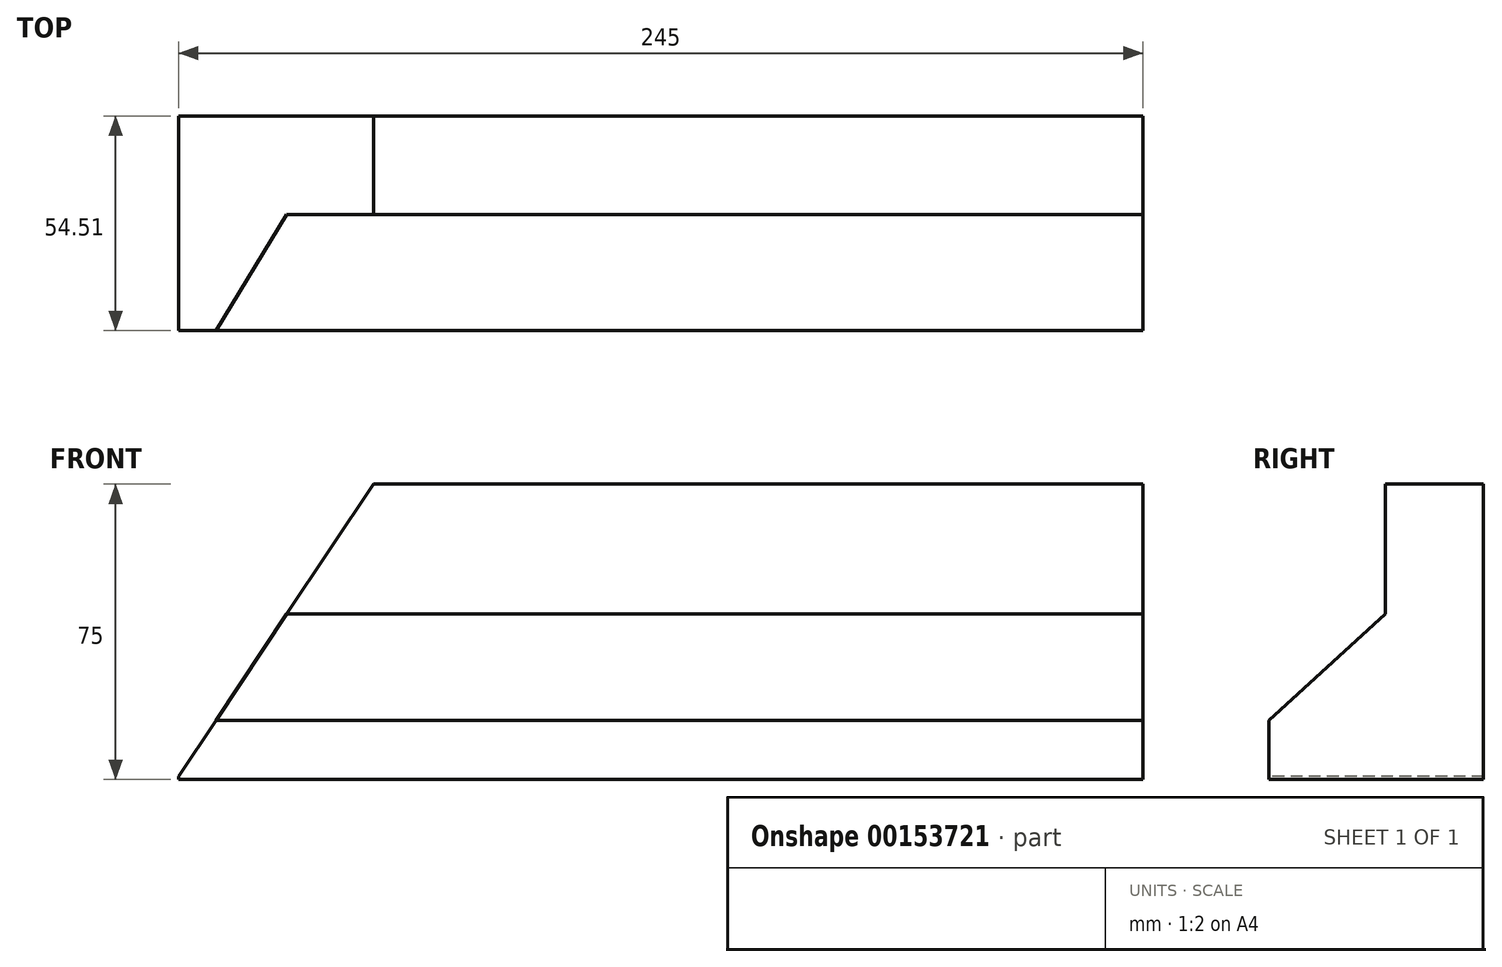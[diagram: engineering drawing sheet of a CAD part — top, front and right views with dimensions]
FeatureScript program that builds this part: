
annotation { "Feature Type Name" : "Feature", "Feature Type Description" : "" }
export const myFeature = defineFeature(function(context is Context, id is Id, definition is map)
    precondition{}
    {
        {
            var Q0;
            Q0=qCreatedBy(makeId("Right.planeOp"),FACE);
            var sketch = newSketch(context, id + "F0", { "sketchPlane" : qUnion([Q0])});
            skLineSegment(sketch, "E0.bottom", {"start": v(-15.45, 41.87) * mm, "end": v(9.55, 41.87) * mm});
            skLineSegment(sketch, "E0.top", {"start": v(-15.45, -33.13) * mm, "end": v(9.55, -33.13) * mm});
            skLineSegment(sketch, "E0.left", {"start": v(-15.45, 41.87) * mm, "end": v(-15.45, -33.13) * mm});
            skLineSegment(sketch, "E0.right", {"start": v(9.55, 41.87) * mm, "end": v(9.55, -33.13) * mm});
            skLineSegment(sketch, "E1.bottom", {"start": v(9.55, -33.13) * mm, "end": v(-44.96, -33.13) * mm});
            skLineSegment(sketch, "E1.top", {"start": v(9.55, -18.13) * mm, "end": v(-44.96, -18.13) * mm});
            skLineSegment(sketch, "E1.left", {"start": v(9.55, -33.13) * mm, "end": v(9.55, -18.13) * mm});
            skLineSegment(sketch, "E1.right", {"start": v(-44.96, -33.13) * mm, "end": v(-44.96, -18.13) * mm});
            skLineSegment(sketch, "E2", {"start": v(-15.45, 8.87) * mm, "end": v(-44.96, -18.13) * mm});
            skSolve(sketch);
        }
        {
            var Q0;
            Q0 = qSketchRegion(id + "F0", true);
            extrude(context, id + "F1", {"entities" : qUnion([Q0]), "endBound" : BoundingType.SYMMETRIC, "depth" : 245 * mm});
        }
        {
            var Q0;
            Q0=qCreatedBy(makeId("Front.planeOp"),FACE);
            var sketch = newSketch(context, id + "F2", { "sketchPlane" : qUnion([Q0])});
            skLineSegment(sketch, "E3", {"start": v(-122.85, 42.13) * mm, "end": v(-72.85, 42.13) * mm});
            skLineSegment(sketch, "E4", {"start": v(-72.85, 42.13) * mm, "end": v(-122.85, -32.87) * mm});
            skLineSegment(sketch, "E5", {"start": v(-122.85, -32.87) * mm, "end": v(-122.85, 42.13) * mm});
            skSolve(sketch);
        }
        {
            var Q0;
            Q0 = qSketchRegion(id + "F2", true);
            extrude(context, id + "F3", {"entities" : qUnion([Q0]), "operationType" : NewBodyOperationType.REMOVE, "endBound" : BoundingType.THROUGH_ALL, "oppositeDirection" : true, "depth" : 25 * mm, "hasSecondDirection" : true, "secondDirectionBound" : SecondDirectionBoundingType.THROUGH_ALL, "secondDirectionOppositeDirection" : false, "secondDirectionDepth" : 25 * mm});
        }
        {
            var Q0;
            Q0=makeQuery(id+"F1.opExtrude","SWEPT_BODY",BODY,{"disambiguationData":[OSD([sQuery(id+"F0.wireOp",EDGE,"E0.bottom"),sQuery(id+"F0.wireOp",EDGE,"E0.left"),sQuery(id+"F0.wireOp",EDGE,"E0.right"),sQuery(id+"F0.wireOp",EDGE,"E1.bottom"),sQuery(id+"F0.wireOp",EDGE,"E1.left"),sQuery(id+"F0.wireOp",EDGE,"E1.right"),sQuery(id+"F0.wireOp",EDGE,"E2")])]});
            transform(context, id + "F4", {"entities" : qUnion([Q0]), "transformType" : TransformType.TRANSLATION_3D, "dx" : 0 * mm, "dy" : 0 * mm, "dz" : 0 * mm, "makeCopy" : true});
        }
    });
